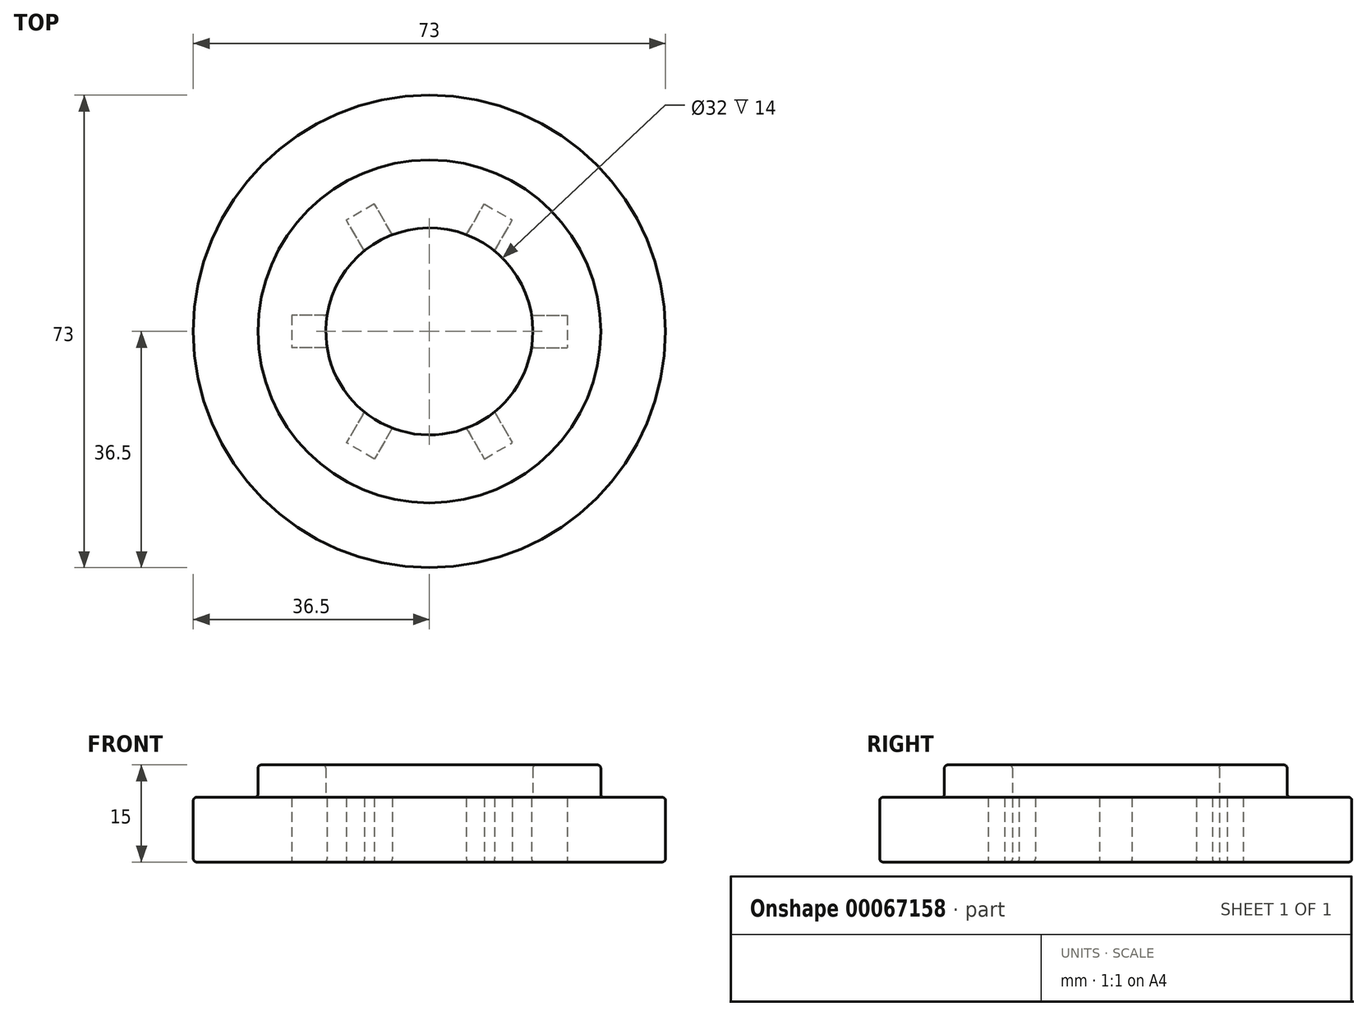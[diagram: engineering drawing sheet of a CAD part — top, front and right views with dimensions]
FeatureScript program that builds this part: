
annotation { "Feature Type Name" : "Feature", "Feature Type Description" : "" }
export const myFeature = defineFeature(function(context is Context, id is Id, definition is map)
    precondition{}
    {
        {
            var Q0;
            Q0=qCreatedBy(makeId("Top.planeOp"),FACE);
            var sketch = newSketch(context, id + "F0", { "sketchPlane" : qUnion([Q0])});
            skCircle(sketch, "E0", {"center": v(0, 0) * mm, "radius": 26.5 * mm});
            skCircle(sketch, "E1", {"center": v(0, 0) * mm, "radius": 16 * mm});
            skCircle(sketch, "E2.cCircle", {"center": v(0, 0) * mm, "radius": 16 * mm, "construction": true});
            skLineSegment(sketch, "E2.0", {"start": v(16, 0) * mm, "end": v(8, -13.86) * mm, "construction": true});
            skLineSegment(sketch, "E2.1", {"start": v(8, -13.86) * mm, "end": v(-8, -13.86) * mm, "construction": true});
            skLineSegment(sketch, "E2.2", {"start": v(-8, -13.86) * mm, "end": v(-16, 0) * mm, "construction": true});
            skLineSegment(sketch, "E2.3", {"start": v(-16, 0) * mm, "end": v(-8, 13.86) * mm, "construction": true});
            skLineSegment(sketch, "E2.4", {"start": v(-8, 13.86) * mm, "end": v(8, 13.86) * mm, "construction": true});
            skLineSegment(sketch, "E2.5", {"start": v(8, 13.86) * mm, "end": v(16, 0) * mm, "construction": true});
            skLineSegment(sketch, "E3", {"start": v(10.45, -18.1) * mm, "end": v(-12.82, 22.2) * mm, "construction": true});
            skLineSegment(sketch, "E4", {"start": v(-10.39, -17.99) * mm, "end": v(10.82, 18.74) * mm, "construction": true});
            skLineSegment(sketch, "E5", {"start": v(21.67, 0) * mm, "end": v(-23.31, 0) * mm, "construction": true});
            skLineSegment(sketch, "E6", {"start": v(-10.07, 12.44) * mm, "end": v(-12.82, 17.2) * mm});
            skLineSegment(sketch, "E7", {"start": v(-5.74, 14.94) * mm, "end": v(-8.49, 19.7) * mm});
            skLineSegment(sketch, "E8", {"start": v(-8.49, 19.7) * mm, "end": v(-12.82, 17.2) * mm});
            skLineSegment(sketch, "E9.MirrorCS", {"start": v(15.8, 2.5) * mm, "end": v(21.3, 2.5) * mm});
            skLineSegment(sketch, "E10.MirrorCS", {"start": v(15.8, -2.5) * mm, "end": v(21.3, -2.5) * mm});
            skLineSegment(sketch, "E11.MirrorCS", {"start": v(21.3, 2.5) * mm, "end": v(21.3, -2.5) * mm});
            skLineSegment(sketch, "E12", {"start": v(0, 23.5) * mm, "end": v(0, -18.62) * mm, "construction": true});
            skLineSegment(sketch, "E13.MirrorCS", {"start": v(5.74, 14.94) * mm, "end": v(8.49, 19.7) * mm});
            skLineSegment(sketch, "E14.MirrorCS", {"start": v(10.07, 12.44) * mm, "end": v(12.82, 17.2) * mm});
            skLineSegment(sketch, "E15.MirrorCS", {"start": v(8.49, 19.7) * mm, "end": v(12.82, 17.2) * mm});
            skLineSegment(sketch, "E16.MirrorCS", {"start": v(10.07, -12.44) * mm, "end": v(12.82, -17.2) * mm});
            skLineSegment(sketch, "E17.MirrorCS", {"start": v(5.74, -14.94) * mm, "end": v(8.49, -19.7) * mm});
            skLineSegment(sketch, "E18.MirrorCS", {"start": v(8.49, -19.7) * mm, "end": v(12.82, -17.2) * mm});
            skLineSegment(sketch, "E19.MirrorCS", {"start": v(-8.49, -19.7) * mm, "end": v(-12.82, -17.2) * mm});
            skLineSegment(sketch, "E20.MirrorCS", {"start": v(-5.74, -14.94) * mm, "end": v(-8.49, -19.7) * mm});
            skLineSegment(sketch, "E21.MirrorCS", {"start": v(-10.07, -12.44) * mm, "end": v(-12.82, -17.2) * mm});
            skLineSegment(sketch, "E22.MirrorCS", {"start": v(-15.8, 2.5) * mm, "end": v(-21.3, 2.5) * mm});
            skLineSegment(sketch, "E23.MirrorCS", {"start": v(-21.3, 2.5) * mm, "end": v(-21.3, -2.5) * mm});
            skLineSegment(sketch, "E24.MirrorCS", {"start": v(-15.8, -2.5) * mm, "end": v(-21.3, -2.5) * mm});
            skCircle(sketch, "E25", {"center": v(0, 0) * mm, "radius": 36.5 * mm});
            skSolve(sketch);
        }
        {
            var Q0;
            Q0=makeQuery(id+"F0.imprint","IMPRINT",FACE,{"disambiguationData":[TD([[makeQuery(id+"F0.imprint","IMPRINT",EDGE,{"derivedFrom":sQuery(id+"F0.wireOp",EDGE,"E0")}),-1.0]])]});
            var Q1;
            Q1=makeQuery(id+"F0.imprint","IMPRINT",FACE,{"disambiguationData":[TD([[makeQuery(id+"F0.imprint","IMPRINT",EDGE,{"derivedFrom":sQuery(id+"F0.wireOp",EDGE,"E0")}),1.0]])]});
            var Q2;
            {var subQ0=sQuery(id+"F0.wireOp",EDGE,"E6");Q2=makeQuery(id+"F0.imprint","IMPRINT",FACE,{"disambiguationData":[TD([[makeQuery(id+"F0.imprint","IMPRINT",EDGE,{"derivedFrom":subQ0}),-1.0]])]});}
            var Q3;
            {var subQ0=sQuery(id+"F0.wireOp",EDGE,"E13.MirrorCS");Q3=makeQuery(id+"F0.imprint","IMPRINT",FACE,{"disambiguationData":[TD([[makeQuery(id+"F0.imprint","IMPRINT",EDGE,{"derivedFrom":subQ0}),-1.0]])]});}
            var Q4;
            Q4=makeQuery(id+"F0.imprint","IMPRINT",FACE,{"disambiguationData":[TD([[makeQuery(id+"F0.imprint","IMPRINT",EDGE,{"derivedFrom":sQuery(id+"F0.wireOp",EDGE,"E11.MirrorCS")}),-1.0]])]});
            var Q5;
            {var subQ0=sQuery(id+"F0.wireOp",EDGE,"E16.MirrorCS");Q5=makeQuery(id+"F0.imprint","IMPRINT",FACE,{"disambiguationData":[TD([[makeQuery(id+"F0.imprint","IMPRINT",EDGE,{"derivedFrom":subQ0}),-1.0]])]});}
            var Q6;
            Q6=makeQuery(id+"F0.imprint","IMPRINT",FACE,{"disambiguationData":[TD([[makeQuery(id+"F0.imprint","IMPRINT",EDGE,{"derivedFrom":sQuery(id+"F0.wireOp",EDGE,"E19.MirrorCS")}),-1.0]])]});
            var Q7;
            {var subQ0=sQuery(id+"F0.wireOp",EDGE,"E22.MirrorCS");Q7=makeQuery(id+"F0.imprint","IMPRINT",FACE,{"disambiguationData":[TD([[makeQuery(id+"F0.imprint","IMPRINT",EDGE,{"derivedFrom":subQ0}),1.0]])]});}
            extrude(context, id + "F1", {"entities" : qUnion([Q0, Q1, Q2, Q3, Q4, Q5, Q6, Q7]), "depth" : 10 * mm});
        }
        {
            var Q0;
            Q0=makeQuery(id+"F0.imprint","IMPRINT",FACE,{"disambiguationData":[TD([[makeQuery(id+"F0.imprint","IMPRINT",EDGE,{"derivedFrom":sQuery(id+"F0.wireOp",EDGE,"E0")}),1.0]])]});
            var Q1;
            {var subQ0=sQuery(id+"F0.wireOp",EDGE,"E6");Q1=makeQuery(id+"F0.imprint","IMPRINT",FACE,{"disambiguationData":[TD([[makeQuery(id+"F0.imprint","IMPRINT",EDGE,{"derivedFrom":subQ0}),-1.0]])]});}
            var Q2;
            {var subQ0=sQuery(id+"F0.wireOp",EDGE,"E13.MirrorCS");Q2=makeQuery(id+"F0.imprint","IMPRINT",FACE,{"disambiguationData":[TD([[makeQuery(id+"F0.imprint","IMPRINT",EDGE,{"derivedFrom":subQ0}),-1.0]])]});}
            var Q3;
            Q3=makeQuery(id+"F0.imprint","IMPRINT",FACE,{"disambiguationData":[TD([[makeQuery(id+"F0.imprint","IMPRINT",EDGE,{"derivedFrom":sQuery(id+"F0.wireOp",EDGE,"E11.MirrorCS")}),-1.0]])]});
            var Q4;
            {var subQ0=sQuery(id+"F0.wireOp",EDGE,"E16.MirrorCS");Q4=makeQuery(id+"F0.imprint","IMPRINT",FACE,{"disambiguationData":[TD([[makeQuery(id+"F0.imprint","IMPRINT",EDGE,{"derivedFrom":subQ0}),-1.0]])]});}
            var Q5;
            Q5=makeQuery(id+"F0.imprint","IMPRINT",FACE,{"disambiguationData":[TD([[makeQuery(id+"F0.imprint","IMPRINT",EDGE,{"derivedFrom":sQuery(id+"F0.wireOp",EDGE,"E19.MirrorCS")}),-1.0]])]});
            var Q6;
            {var subQ0=sQuery(id+"F0.wireOp",EDGE,"E22.MirrorCS");Q6=makeQuery(id+"F0.imprint","IMPRINT",FACE,{"disambiguationData":[TD([[makeQuery(id+"F0.imprint","IMPRINT",EDGE,{"derivedFrom":subQ0}),1.0]])]});}
            extrude(context, id + "F2", {"entities" : qUnion([Q0, Q1, Q2, Q3, Q4, Q5, Q6]), "operationType" : NewBodyOperationType.ADD, "depth" : 15 * mm});
        }
        {
            var Q0;
            {var subQ0=sQuery(id+"F0.wireOp",EDGE,"E13.MirrorCS");Q0=makeQuery(id+"F0.imprint","IMPRINT",FACE,{"disambiguationData":[TD([[makeQuery(id+"F0.imprint","IMPRINT",EDGE,{"derivedFrom":subQ0}),-1.0]])]});}
            var Q1;
            {var subQ0=sQuery(id+"F0.wireOp",EDGE,"E6");Q1=makeQuery(id+"F0.imprint","IMPRINT",FACE,{"disambiguationData":[TD([[makeQuery(id+"F0.imprint","IMPRINT",EDGE,{"derivedFrom":subQ0}),-1.0]])]});}
            var Q2;
            {var subQ0=sQuery(id+"F0.wireOp",EDGE,"E22.MirrorCS");Q2=makeQuery(id+"F0.imprint","IMPRINT",FACE,{"disambiguationData":[TD([[makeQuery(id+"F0.imprint","IMPRINT",EDGE,{"derivedFrom":subQ0}),1.0]])]});}
            var Q3;
            Q3=makeQuery(id+"F0.imprint","IMPRINT",FACE,{"disambiguationData":[TD([[makeQuery(id+"F0.imprint","IMPRINT",EDGE,{"derivedFrom":sQuery(id+"F0.wireOp",EDGE,"E19.MirrorCS")}),-1.0]])]});
            var Q4;
            {var subQ0=sQuery(id+"F0.wireOp",EDGE,"E16.MirrorCS");Q4=makeQuery(id+"F0.imprint","IMPRINT",FACE,{"disambiguationData":[TD([[makeQuery(id+"F0.imprint","IMPRINT",EDGE,{"derivedFrom":subQ0}),-1.0]])]});}
            var Q5;
            Q5=makeQuery(id+"F0.imprint","IMPRINT",FACE,{"disambiguationData":[TD([[makeQuery(id+"F0.imprint","IMPRINT",EDGE,{"derivedFrom":sQuery(id+"F0.wireOp",EDGE,"E11.MirrorCS")}),-1.0]])]});
            extrude(context, id + "F3", {"entities" : qUnion([Q0, Q1, Q2, Q3, Q4, Q5]), "operationType" : NewBodyOperationType.REMOVE, "depth" : 10 * mm});
        }
        {
            var Q0;
            Q0=makeQuery(id+"F2.boolean.opBoolean","INTERSECT",EDGE,{"derivedFrom":[makeQuery(id+"F1.opExtrude","CAP_FACE",FACE,{"disambiguationData":[OSD([sQuery(id+"F0.wireOp",EDGE,"E1"),sQuery(id+"F0.wireOp",EDGE,"E25")])],"isStart":false}),makeQuery(id+"F2.opExtrude","SWEPT_FACE",FACE,{"disambiguationData":[OSD([sQuery(id+"F0.wireOp",EDGE,"E0")])]})]});
            var Q1;
            Q1=makeQuery(id+"F1.opExtrude","CAP_EDGE",EDGE,{"disambiguationData":[OSD([sQuery(id+"F0.wireOp",EDGE,"E25")])],"isStart":false});
            var Q2;
            Q2=makeQuery(id+"F2.opExtrude","CAP_EDGE",EDGE,{"disambiguationData":[OSD([sQuery(id+"F0.wireOp",EDGE,"E0")])],"isStart":false});
            var Q3;
            Q3=makeQuery(id+"F2.opExtrude","CAP_EDGE",EDGE,{"disambiguationData":[OSD([sQuery(id+"F0.wireOp",EDGE,"E1")])],"isStart":false});
            var Q4;
            Q4=makeQuery(id+"F1.opExtrude","CAP_EDGE",EDGE,{"disambiguationData":[OSD([sQuery(id+"F0.wireOp",EDGE,"E25")])],"isStart":true});
            var Q5;
            {var subQ0=sQuery(id+"F0.wireOp",EDGE,"E1");Q5=makeQuery(id+"F3.boolean.opBoolean","SPLIT",EDGE,{"disambiguationData":[TD([makeQuery(id+"F3.opExtrude","SWEPT_FACE",FACE,{"disambiguationData":[OSD([sQuery(id+"F0.wireOp",EDGE,"E16.MirrorCS")])]})])],"derivedFrom":makeQuery(id+"F1.opExtrude","CAP_EDGE",EDGE,{"disambiguationData":[OSD([subQ0])],"isStart":true})});}
            var Q6;
            {var subQ0=sQuery(id+"F0.wireOp",EDGE,"E1");Q6=makeQuery(id+"F3.boolean.opBoolean","SPLIT",EDGE,{"disambiguationData":[TD([makeQuery(id+"F3.opExtrude","SWEPT_FACE",FACE,{"disambiguationData":[OSD([sQuery(id+"F0.wireOp",EDGE,"E17.MirrorCS")])]})])],"derivedFrom":makeQuery(id+"F1.opExtrude","CAP_EDGE",EDGE,{"disambiguationData":[OSD([subQ0])],"isStart":true})});}
            var Q7;
            {var subQ0=sQuery(id+"F0.wireOp",EDGE,"E1");Q7=makeQuery(id+"F3.boolean.opBoolean","SPLIT",EDGE,{"disambiguationData":[TD([makeQuery(id+"F3.opExtrude","SWEPT_FACE",FACE,{"disambiguationData":[OSD([sQuery(id+"F0.wireOp",EDGE,"E21.MirrorCS")])]})])],"derivedFrom":makeQuery(id+"F1.opExtrude","CAP_EDGE",EDGE,{"disambiguationData":[OSD([subQ0])],"isStart":true})});}
            var Q8;
            {var subQ0=sQuery(id+"F0.wireOp",EDGE,"E1");Q8=makeQuery(id+"F3.boolean.opBoolean","SPLIT",EDGE,{"disambiguationData":[TD([makeQuery(id+"F3.opExtrude","SWEPT_FACE",FACE,{"disambiguationData":[OSD([sQuery(id+"F0.wireOp",EDGE,"E6")])]})])],"derivedFrom":makeQuery(id+"F1.opExtrude","CAP_EDGE",EDGE,{"disambiguationData":[OSD([subQ0])],"isStart":true})});}
            var Q9;
            {var subQ0=sQuery(id+"F0.wireOp",EDGE,"E1");Q9=makeQuery(id+"F3.boolean.opBoolean","SPLIT",EDGE,{"disambiguationData":[TD([makeQuery(id+"F3.opExtrude","SWEPT_FACE",FACE,{"disambiguationData":[OSD([sQuery(id+"F0.wireOp",EDGE,"E7")])]})])],"derivedFrom":makeQuery(id+"F1.opExtrude","CAP_EDGE",EDGE,{"disambiguationData":[OSD([subQ0])],"isStart":true})});}
            var Q10;
            {var subQ0=sQuery(id+"F0.wireOp",EDGE,"E1");Q10=makeQuery(id+"F3.boolean.opBoolean","SPLIT",EDGE,{"disambiguationData":[TD([makeQuery(id+"F3.opExtrude","SWEPT_FACE",FACE,{"disambiguationData":[OSD([sQuery(id+"F0.wireOp",EDGE,"E9.MirrorCS")])]})])],"derivedFrom":makeQuery(id+"F1.opExtrude","CAP_EDGE",EDGE,{"disambiguationData":[OSD([subQ0])],"isStart":true})});}
            var Q11;
            Q11=makeQuery(id+"F3.boolean.opBoolean","COPY",EDGE,{"derivedFrom":makeQuery(id+"F3.opExtrude","CAP_EDGE",EDGE,{"disambiguationData":[OSD([sQuery(id+"F0.wireOp",EDGE,"E20.MirrorCS")])],"isStart":true})});
            var Q12;
            Q12=makeQuery(id+"F3.boolean.opBoolean","COPY",EDGE,{"derivedFrom":makeQuery(id+"F3.opExtrude","CAP_EDGE",EDGE,{"disambiguationData":[OSD([sQuery(id+"F0.wireOp",EDGE,"E19.MirrorCS")])],"isStart":true})});
            var Q13;
            Q13=makeQuery(id+"F3.boolean.opBoolean","COPY",EDGE,{"derivedFrom":makeQuery(id+"F3.opExtrude","CAP_EDGE",EDGE,{"disambiguationData":[OSD([sQuery(id+"F0.wireOp",EDGE,"E21.MirrorCS")])],"isStart":true})});
            var Q14;
            Q14=makeQuery(id+"F3.boolean.opBoolean","COPY",EDGE,{"derivedFrom":makeQuery(id+"F3.opExtrude","CAP_EDGE",EDGE,{"disambiguationData":[OSD([sQuery(id+"F0.wireOp",EDGE,"E24.MirrorCS")])],"isStart":true})});
            var Q15;
            Q15=makeQuery(id+"F3.boolean.opBoolean","COPY",EDGE,{"derivedFrom":makeQuery(id+"F3.opExtrude","CAP_EDGE",EDGE,{"disambiguationData":[OSD([sQuery(id+"F0.wireOp",EDGE,"E23.MirrorCS")])],"isStart":true})});
            var Q16;
            Q16=makeQuery(id+"F3.boolean.opBoolean","COPY",EDGE,{"derivedFrom":makeQuery(id+"F3.opExtrude","CAP_EDGE",EDGE,{"disambiguationData":[OSD([sQuery(id+"F0.wireOp",EDGE,"E22.MirrorCS")])],"isStart":true})});
            var Q17;
            Q17=makeQuery(id+"F3.boolean.opBoolean","COPY",EDGE,{"derivedFrom":makeQuery(id+"F3.opExtrude","CAP_EDGE",EDGE,{"disambiguationData":[OSD([sQuery(id+"F0.wireOp",EDGE,"E6")])],"isStart":true})});
            var Q18;
            Q18=makeQuery(id+"F3.boolean.opBoolean","COPY",EDGE,{"derivedFrom":makeQuery(id+"F3.opExtrude","CAP_EDGE",EDGE,{"disambiguationData":[OSD([sQuery(id+"F0.wireOp",EDGE,"E8")])],"isStart":true})});
            var Q19;
            Q19=makeQuery(id+"F3.boolean.opBoolean","COPY",EDGE,{"derivedFrom":makeQuery(id+"F3.opExtrude","CAP_EDGE",EDGE,{"disambiguationData":[OSD([sQuery(id+"F0.wireOp",EDGE,"E7")])],"isStart":true})});
            var Q20;
            Q20=makeQuery(id+"F3.boolean.opBoolean","COPY",EDGE,{"derivedFrom":makeQuery(id+"F3.opExtrude","CAP_EDGE",EDGE,{"disambiguationData":[OSD([sQuery(id+"F0.wireOp",EDGE,"E13.MirrorCS")])],"isStart":true})});
            var Q21;
            Q21=makeQuery(id+"F3.boolean.opBoolean","COPY",EDGE,{"derivedFrom":makeQuery(id+"F3.opExtrude","CAP_EDGE",EDGE,{"disambiguationData":[OSD([sQuery(id+"F0.wireOp",EDGE,"E15.MirrorCS")])],"isStart":true})});
            var Q22;
            Q22=makeQuery(id+"F3.boolean.opBoolean","COPY",EDGE,{"derivedFrom":makeQuery(id+"F3.opExtrude","CAP_EDGE",EDGE,{"disambiguationData":[OSD([sQuery(id+"F0.wireOp",EDGE,"E14.MirrorCS")])],"isStart":true})});
            var Q23;
            Q23=makeQuery(id+"F3.boolean.opBoolean","COPY",EDGE,{"derivedFrom":makeQuery(id+"F3.opExtrude","CAP_EDGE",EDGE,{"disambiguationData":[OSD([sQuery(id+"F0.wireOp",EDGE,"E10.MirrorCS")])],"isStart":true})});
            var Q24;
            Q24=makeQuery(id+"F3.boolean.opBoolean","COPY",EDGE,{"derivedFrom":makeQuery(id+"F3.opExtrude","CAP_EDGE",EDGE,{"disambiguationData":[OSD([sQuery(id+"F0.wireOp",EDGE,"E11.MirrorCS")])],"isStart":true})});
            var Q25;
            Q25=makeQuery(id+"F3.boolean.opBoolean","COPY",EDGE,{"derivedFrom":makeQuery(id+"F3.opExtrude","CAP_EDGE",EDGE,{"disambiguationData":[OSD([sQuery(id+"F0.wireOp",EDGE,"E9.MirrorCS")])],"isStart":true})});
            var Q26;
            Q26=makeQuery(id+"F3.boolean.opBoolean","COPY",EDGE,{"derivedFrom":makeQuery(id+"F3.opExtrude","CAP_EDGE",EDGE,{"disambiguationData":[OSD([sQuery(id+"F0.wireOp",EDGE,"E16.MirrorCS")])],"isStart":true})});
            var Q27;
            Q27=makeQuery(id+"F3.boolean.opBoolean","COPY",EDGE,{"derivedFrom":makeQuery(id+"F3.opExtrude","CAP_EDGE",EDGE,{"disambiguationData":[OSD([sQuery(id+"F0.wireOp",EDGE,"E18.MirrorCS")])],"isStart":true})});
            var Q28;
            Q28=makeQuery(id+"F3.boolean.opBoolean","COPY",EDGE,{"derivedFrom":makeQuery(id+"F3.opExtrude","CAP_EDGE",EDGE,{"disambiguationData":[OSD([sQuery(id+"F0.wireOp",EDGE,"E17.MirrorCS")])],"isStart":true})});
            fillet(context, id + "F4", {"entities" : qUnion([Q0, Q1, Q2, Q3, Q4, Q5, Q6, Q7, Q8, Q9, Q10, Q11, Q12, Q13, Q14, Q15, Q16, Q17, Q18, Q19, Q20, Q21, Q22, Q23, Q24, Q25, Q26, Q27, Q28]), "radius" : 0.5 * mm, "tangentPropagation" : true, "allowEdgeOverflow" : false});
        }
    });
